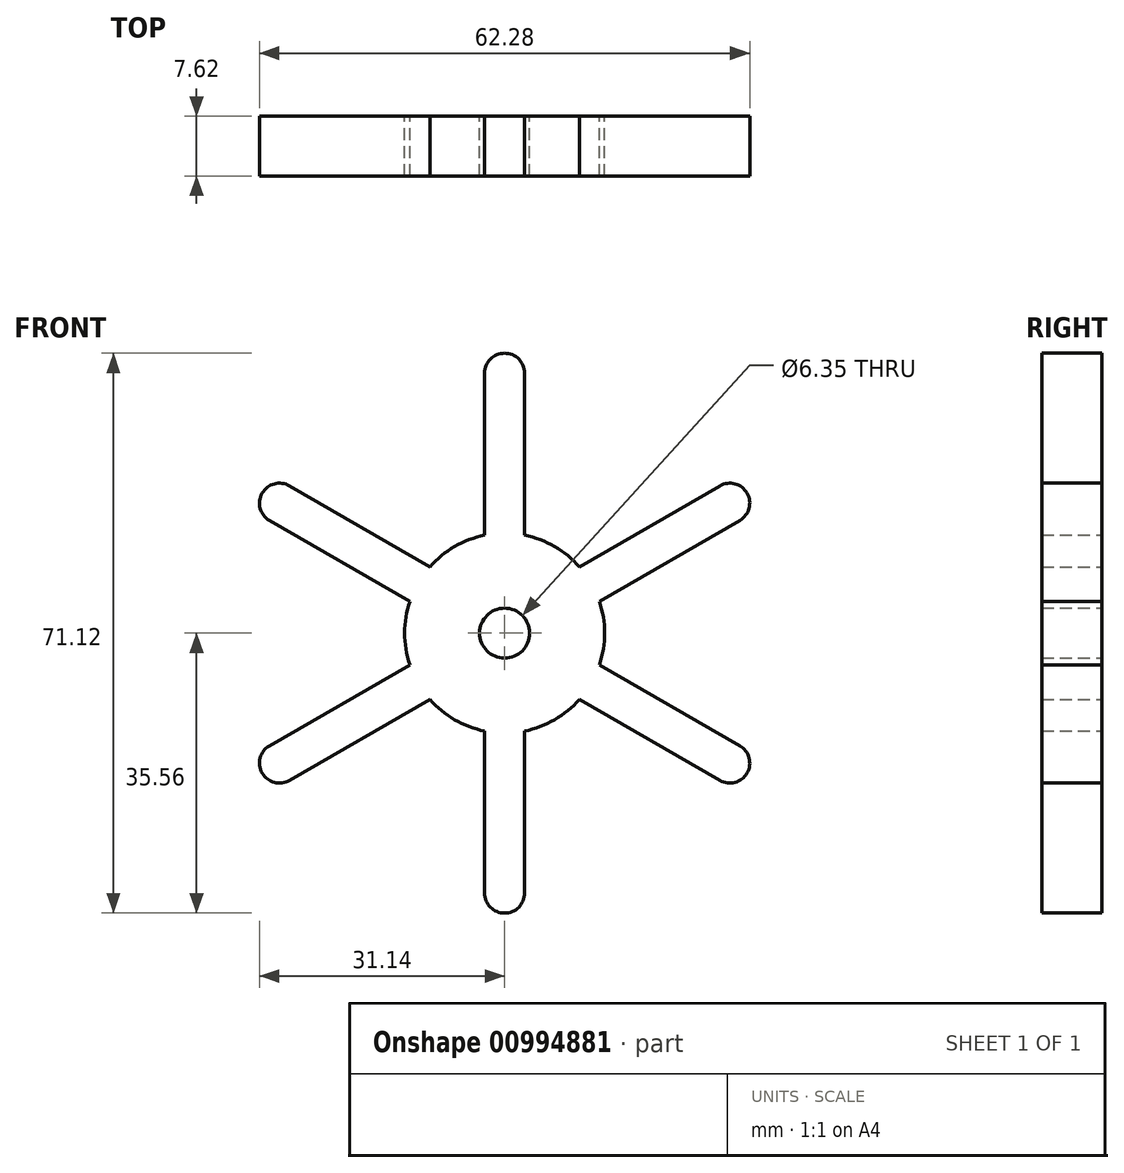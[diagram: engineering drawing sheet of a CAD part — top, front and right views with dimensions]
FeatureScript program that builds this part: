
annotation { "Feature Type Name" : "Feature", "Feature Type Description" : "" }
export const myFeature = defineFeature(function(context is Context, id is Id, definition is map)
    precondition{}
    {
        {
            var Q0;
            Q0=qCreatedBy(makeId("Front.planeOp"),FACE);
            var sketch = newSketch(context, id + "F0", { "sketchPlane" : qUnion([Q0])});
            skCircle(sketch, "E0", {"center": v(0, 0) * mm, "radius": 12.7 * mm});
            skLineSegment(sketch, "E1", {"start": v(-2.54, 33.02) * mm, "end": v(2.54, 33.02) * mm});
            skLineSegment(sketch, "E2", {"start": v(2.54, 33.02) * mm, "end": v(2.54, 12.44) * mm});
            skArc(sketch, "E3", {"start": v(2.54, 33.02) * mm, "mid": v(0, 35.56) * mm, "end": v(-2.54, 33.02) * mm});
            skArc(sketch, "E4.1.0", {"start": v(-27.33, 18.7) * mm, "mid": v(-30.8, 17.78) * mm, "end": v(-29.87, 14.31) * mm});
            skLineSegment(sketch, "E4.1.2", {"start": v(-27.33, 18.7) * mm, "end": v(-9.5, 8.42) * mm});
            skArc(sketch, "E4.2.0", {"start": v(-29.87, -14.31) * mm, "mid": v(-30.8, -17.78) * mm, "end": v(-27.33, -18.7) * mm});
            skLineSegment(sketch, "E4.2.2", {"start": v(-29.87, -14.31) * mm, "end": v(-12.05, -4.02) * mm});
            skArc(sketch, "E4.3.0", {"start": v(-2.54, -33.02) * mm, "mid": v(0, -35.56) * mm, "end": v(2.54, -33.02) * mm});
            skLineSegment(sketch, "E4.3.2", {"start": v(-2.54, -33.02) * mm, "end": v(-2.54, -12.44) * mm});
            skArc(sketch, "E4.4.0", {"start": v(27.33, -18.7) * mm, "mid": v(30.8, -17.78) * mm, "end": v(29.87, -14.31) * mm});
            skLineSegment(sketch, "E4.4.2", {"start": v(27.33, -18.7) * mm, "end": v(9.5, -8.42) * mm});
            skArc(sketch, "E4.5.0", {"start": v(29.87, 14.31) * mm, "mid": v(30.8, 17.78) * mm, "end": v(27.33, 18.7) * mm});
            skLineSegment(sketch, "E4.5.2", {"start": v(29.87, 14.31) * mm, "end": v(12.05, 4.02) * mm});
            skLineSegment(sketch, "E5.trimOffspring", {"start": v(-2.54, 12.44) * mm, "end": v(-2.54, 33.02) * mm});
            skLineSegment(sketch, "E6.trimOffspring", {"start": v(9.5, 8.42) * mm, "end": v(27.33, 18.7) * mm});
            skLineSegment(sketch, "E7.trimOffspring", {"start": v(12.05, -4.02) * mm, "end": v(29.87, -14.31) * mm});
            skLineSegment(sketch, "E8.trimOffspring", {"start": v(2.54, -12.44) * mm, "end": v(2.54, -33.02) * mm});
            skLineSegment(sketch, "E9.trimOffspring", {"start": v(-9.5, -8.42) * mm, "end": v(-27.33, -18.7) * mm});
            skLineSegment(sketch, "E10.trimOffspring", {"start": v(-12.05, 4.02) * mm, "end": v(-29.87, 14.31) * mm});
            skCircle(sketch, "E11", {"center": v(0, 0) * mm, "radius": 3.18 * mm});
            skSolve(sketch);
        }
        {
            var Q0;
            Q0 = qSketchRegion(id + "F0", true);
            extrude(context, id + "F1", {"entities" : qUnion([Q0]), "depth" : 7.62 * mm, "offsetDistance" : 25.4 * mm});
        }
    });
